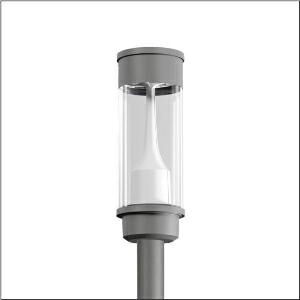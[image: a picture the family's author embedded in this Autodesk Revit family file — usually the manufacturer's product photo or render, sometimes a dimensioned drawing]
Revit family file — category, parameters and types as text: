
# Revit family: litepole_iq___p1_0a_5xa5415nf14h_8c95
name_source: partatom
category: Lighting Fixtures
units: mm (PartAtom-declared; Revit-internal decimal feet)

## family parameters
Cut with Voids When Loaded = No
Host = Face
Light Source = No
Part Type = Normal
Room Calculation Point = No
Round Connector Dimension = Use Diameter
Shared = No

## types (1)
- --- (1 x LED, 1510 lm, 11.8 W, 2700K)
    Apparent Load = 12 VA
    CIE Flux Codes = 32 61 90 93 100
    Color Rendering = 70
    Color Temperature = 2700K
    Default Elevation = 1800 mm
    Description = Litepole iQ, mast luminaire, Module 540 iQ-SR, primary light control with 3 zone facetted reflector, of plastic, silver coated, highly specular, structured, primary optical cover: cover, of PMMA, transparent, partly coated, light distribution: P1.0a, light emission: direct distribution, primary light characteristic: strongly asymmetric, installation type: post-top, LED, High Power LED, rated luminous flux: 1.510lm, luminous efficacy: 128lm/W, light colour: 727, colour temperature: 2700K, control gear: ECG iQ, control: optimised constant luminous flux control (CLO 2.0), Desk-Remote (wireless, voltage-free reading and setting of iQ features in the workshop via application-optimized NFC function/RFID function), Light-Fading, Smart-Wire, Night-Set, Lumen-Switch, Temp-Guard, Auto-Match, Street-Remote, presetting dimming logarithmic, with terminal, 6-pole, max. 2.5mm², mains connection: 230..240V, AC, 50/60Hz, start of lifetime: 12W, end of service life: 12W, reduction: 6W, luminaire housing, upper part, of glass-fibre reinforced polyester, coated, Siteco® metallic grey (DB 702S), diameter: 210mm, height: 590mm, spigot size: d x l = 76 x 70mm (post-top) | with reducer (optional accessory) 60 x 70mm, post-top mast mounting element, of diecast aluminium, coated, Siteco® metallic grey (DB 702S), Module 540 iQ-SR, traffic white (RAL 9016), equipment: standard, protection rating (complete): IP65, insulation class (complete): insulation class II (safety insulation), certification: CE, ENEC, VDE, packaging unit: 1 piece

Light Distribution: P1.0a
    Height = 590 mm
    Lamp = 1 x LED
    Lamp Light Flux = 1510 lm
    Lamp Power = 11.8 W
    Lamp count = 1
    Length = 220 mm
    Luminous efficacy = 128 lm/W
    Manufacturer = Siteco
    ModVariant = No
    Model = 5XA5415NF14H
    Number of Poles = 1
    OnlyDefault = Yes
    Power Factor = 1
    Product Name = Litepole iQ | P1.0a
    Product group = mast luminaire | pylon top
    ProductGroupID = 6100
    Protection Class = Protection class II
    Protection Degree = IP 65
    RLX_Detail_Level = 1
    RLX_Emergency_Light_Flux = 0 lm
    RLX_Emergency_Type = 0
    RLX_Emergency_Type_DB = No
    RlxData = <blob elided: 63937 chars, md5=801eed24>
    Socket = socket
    Standby Power = 0 W
    System Light Flux = 1510 lm
    System Power = 12 W
    Type Comments = factory setting: luminous flux: 100 % | dim-lin: 254 | 472 mA
    Type Image = l_1006025.jpg
    URL = http://relux.com
    VarID = @adj_085295
    Voltage = 0 V
    Weight = 0.00 kg
    Width = 0 mm  [stored 0 ft]

note: [stored X ft] marks values corroborated as IEEE doubles in the binary element streams (Revit-internal decimal feet)

## geometry (parser evidence)
native form markers: Blend x4, Sweep x11
no freeform markers — native parametric forms only
